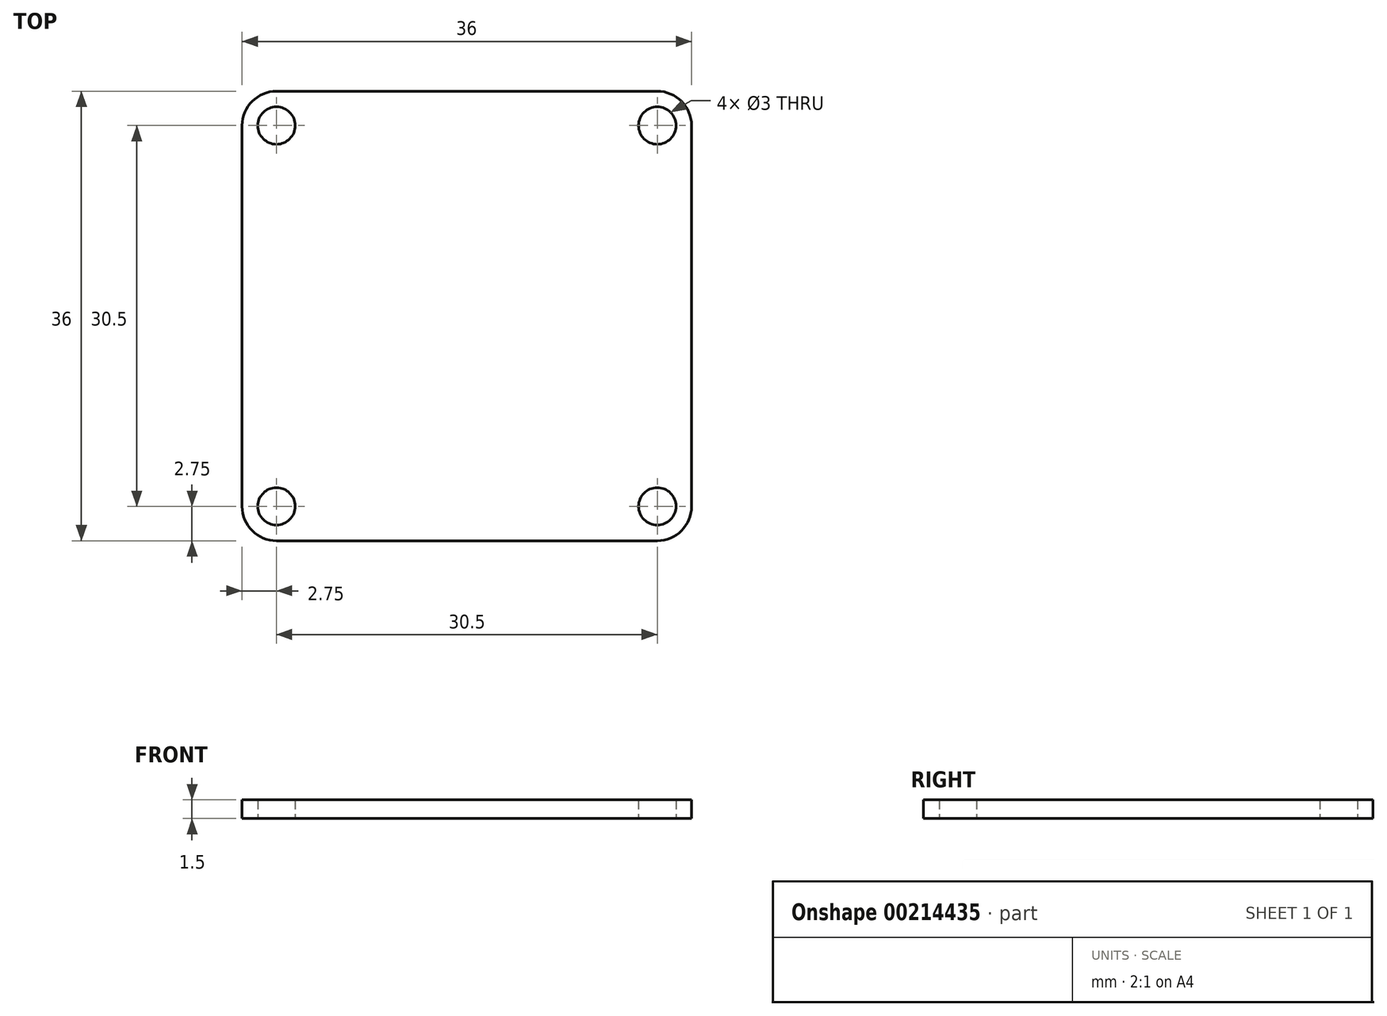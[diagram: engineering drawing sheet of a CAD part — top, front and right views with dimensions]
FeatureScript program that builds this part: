
annotation { "Feature Type Name" : "Feature", "Feature Type Description" : "" }
export const myFeature = defineFeature(function(context is Context, id is Id, definition is map)
    precondition{}
    {
        {
            var Q0;
            Q0=qCreatedBy(makeId("Top.planeOp"),FACE);
            var sketch = newSketch(context, id + "F0", { "sketchPlane" : qUnion([Q0])});
            skLineSegment(sketch, "E0.bottom", {"start": v(-15.25, 18) * mm, "end": v(15.25, 18) * mm});
            skLineSegment(sketch, "E0.top", {"start": v(-15.25, -18) * mm, "end": v(15.25, -18) * mm});
            skLineSegment(sketch, "E0.left", {"start": v(-18, 15.25) * mm, "end": v(-18, -15.25) * mm});
            skLineSegment(sketch, "E0.right", {"start": v(18, 15.25) * mm, "end": v(18, -15.25) * mm});
            skLineSegment(sketch, "E1.bottom", {"start": v(-15.25, 15.25) * mm, "end": v(15.25, 15.25) * mm, "construction": true});
            skLineSegment(sketch, "E1.top", {"start": v(-15.25, -15.25) * mm, "end": v(15.25, -15.25) * mm, "construction": true});
            skLineSegment(sketch, "E1.left", {"start": v(-15.25, 15.25) * mm, "end": v(-15.25, -15.25) * mm, "construction": true});
            skLineSegment(sketch, "E1.right", {"start": v(15.25, 15.25) * mm, "end": v(15.25, -15.25) * mm, "construction": true});
            skCircle(sketch, "E2", {"center": v(-15.25, 15.25) * mm, "radius": 1.5 * mm});
            skCircle(sketch, "E3", {"center": v(15.25, 15.25) * mm, "radius": 1.5 * mm});
            skCircle(sketch, "E4", {"center": v(15.25, -15.25) * mm, "radius": 1.5 * mm});
            skCircle(sketch, "E5", {"center": v(-15.25, -15.25) * mm, "radius": 1.5 * mm});
            skPoint(sketch, "E6.visualSharp", {"position": v(-18, 18) * mm});
            skArc(sketch, "E6.filletArc", {"start": v(-15.25, 18) * mm, "mid": v(-17.2, 17.2) * mm, "end": v(-18, 15.25) * mm});
            skPoint(sketch, "E7.visualSharp", {"position": v(18, 18) * mm});
            skArc(sketch, "E7.filletArc", {"start": v(18, 15.25) * mm, "mid": v(17.2, 17.2) * mm, "end": v(15.25, 18) * mm});
            skPoint(sketch, "E8.visualSharp", {"position": v(18, -18) * mm});
            skArc(sketch, "E8.filletArc", {"start": v(15.25, -18) * mm, "mid": v(17.2, -17.2) * mm, "end": v(18, -15.25) * mm});
            skPoint(sketch, "E9.visualSharp", {"position": v(-18, -18) * mm});
            skArc(sketch, "E9.filletArc", {"start": v(-18, -15.25) * mm, "mid": v(-17.2, -17.2) * mm, "end": v(-15.25, -18) * mm});
            skSolve(sketch);
        }
        {
            var Q0;
            Q0 = qSketchRegion(id + "F0", true);
            extrude(context, id + "F1", {"entities" : qUnion([Q0]), "depth" : 1.5 * mm});
        }
    });
